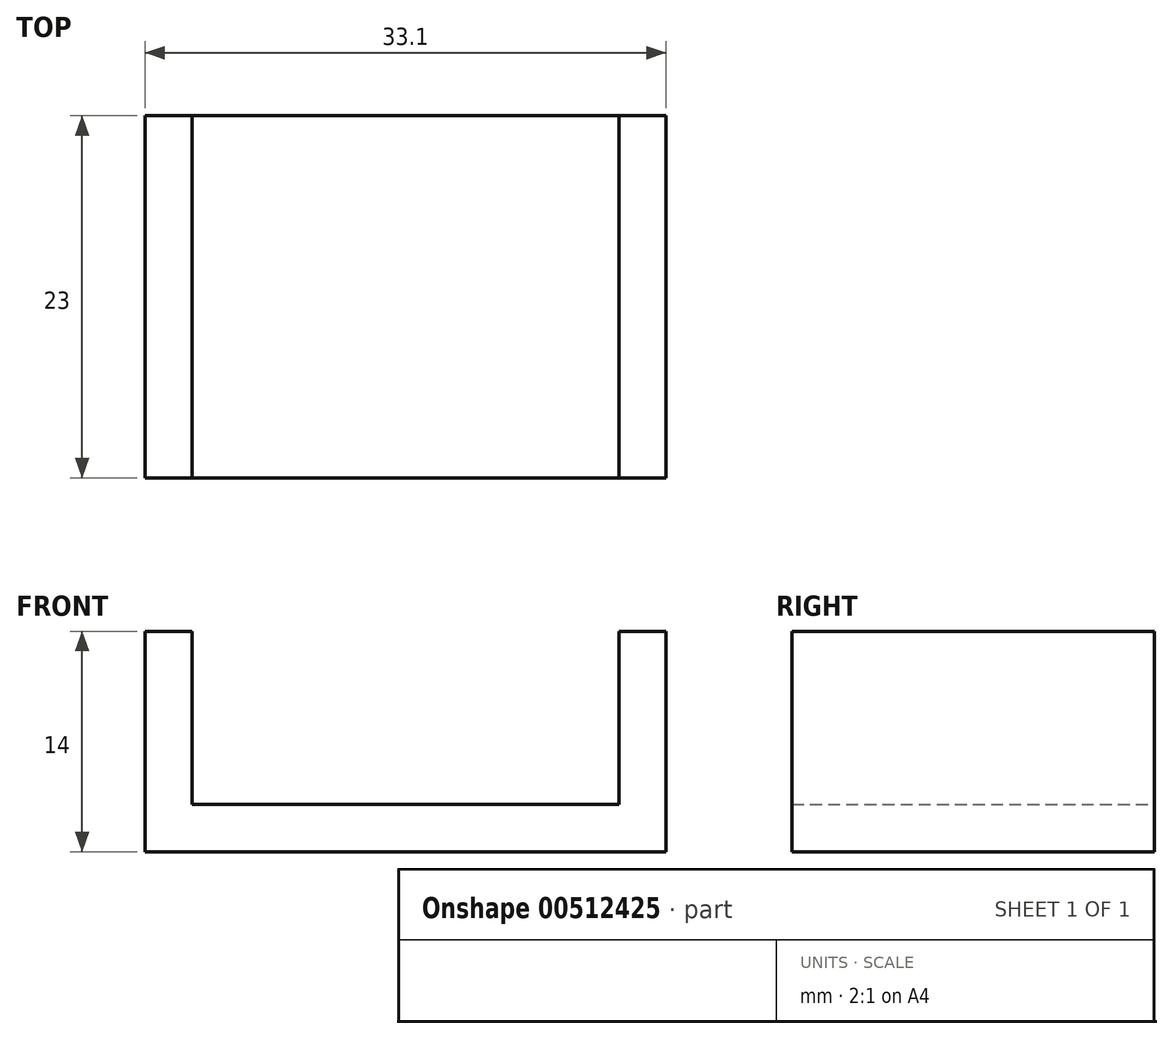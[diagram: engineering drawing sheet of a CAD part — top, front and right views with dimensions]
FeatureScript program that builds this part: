
annotation { "Feature Type Name" : "Feature", "Feature Type Description" : "" }
export const myFeature = defineFeature(function(context is Context, id is Id, definition is map)
    precondition{}
    {
        {
            var Q0;
            Q0=qCreatedBy(makeId("Front.planeOp"),FACE);
            var sketch = newSketch(context, id + "F0", { "sketchPlane" : qUnion([Q0])});
            skLineSegment(sketch, "E0.top", {"start": v(-52.7, -55.81) * mm, "end": v(-25.6, -55.81) * mm});
            skLineSegment(sketch, "E0.left", {"start": v(-52.7, -44.81) * mm, "end": v(-52.7, -55.81) * mm});
            skLineSegment(sketch, "E0.right", {"start": v(-25.6, -44.81) * mm, "end": v(-25.6, -55.81) * mm});
            skLineSegment(sketch, "E1.0", {"start": v(-22.6, -44.81) * mm, "end": v(-22.6, -58.81) * mm});
            skLineSegment(sketch, "E1.1", {"start": v(-55.7, -58.81) * mm, "end": v(-22.6, -58.81) * mm});
            skLineSegment(sketch, "E1.2", {"start": v(-55.7, -44.81) * mm, "end": v(-55.7, -58.81) * mm});
            skLineSegment(sketch, "E2", {"start": v(-55.7, -44.81) * mm, "end": v(-52.7, -44.81) * mm});
            skLineSegment(sketch, "E3", {"start": v(-25.6, -44.81) * mm, "end": v(-22.6, -44.81) * mm});
            skSolve(sketch);
        }
        {
            var Q0;
            Q0 = qSketchRegion(id + "F0", true);
            extrude(context, id + "F1", {"entities" : qUnion([Q0]), "depth" : 23 * mm});
        }
    });
